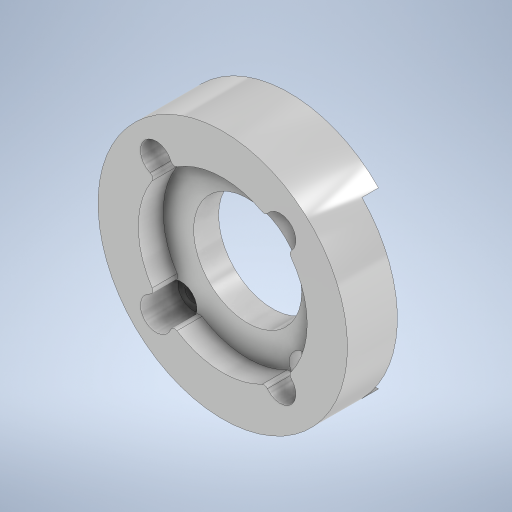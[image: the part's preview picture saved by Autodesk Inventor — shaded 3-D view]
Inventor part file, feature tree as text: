
AUTODESK INVENTOR PART (.ipt)
format: ipt  version: 2024.2 (Build 282272000, 272)  size: 334,336 bytes
history: native  units: in
note: dims shown in document units (in); Inventor stores cm internally (conversion verified against a paired STEP export)
features: sketch x6, extrude x5, hole x1, fillet x1
ambient origin geometry x8: Origin, YZ Plane, XZ Plane, XY Plane, X Axis, Y Axis, Z Axis, Center Point
bodies: Body1 (feature_tree)
feature tree (13):
  extrude  "Extrusion7"  Depth=0.315in TaperAngle=0.0deg
  extrude  "Extrusion8"  Depth=0.0787in TaperAngle=0.0deg
  extrude  "Extrusion9"  Depth=0.1181in TaperAngle=0.0deg
  extrude  "Extrusion11"  Depth=0.315in
  hole  "Hole2"  [1 undecoded]
  extrude  "Extrusion12"  Depth=0.0157in
  fillet  "Fillet2"  [1 undecoded]
  sketch  "Sketch8"  dims[d33=1.1811in d34=0.315in d35=0.0in]
  sketch  "Sketch10"  dims[d37=0.0787in d38=0.0in d39=0.0433in d40=0.0in]
  sketch  "Sketch11"  dims[d44=0.0079in d45=0.1181in d46=0.0in]
  sketch  "Sketch13"  dims[d47=0.0827in d48=0.2362in d49=0.1575in d50=0.0787in d51=90.0deg d52=0.315in d53=0.8108in d54=0.1496in]
  sketch  "Sketch14"  dims[d55=0.1772in d56=0.0in d57=0.0197in]
  sketch  "Sketch15"  dims[d58=0.5118in d59=0.0157in]
note: 2 required parameter values undecoded (feature->parameter linkage not recoverable at this tier; creation-order binding heuristic only, values carry confidence <= 0.55)
